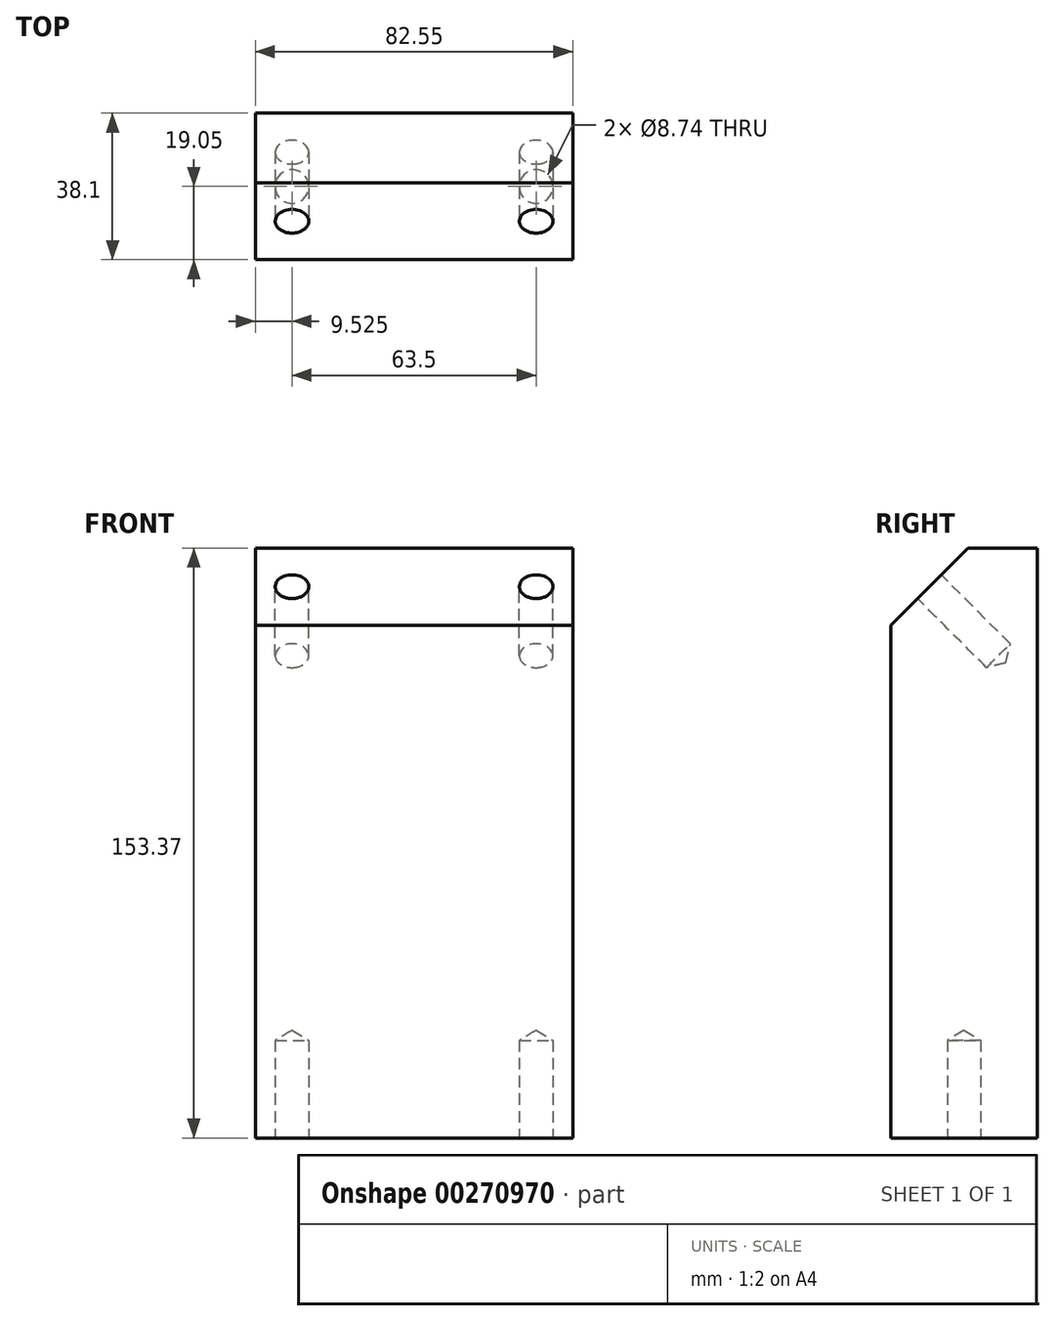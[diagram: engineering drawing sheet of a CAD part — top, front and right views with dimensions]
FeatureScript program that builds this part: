
annotation { "Feature Type Name" : "Feature", "Feature Type Description" : "" }
export const myFeature = defineFeature(function(context is Context, id is Id, definition is map)
    precondition{}
    {
        {
            var Q0;
            Q0=qCreatedBy(makeId("Top.planeOp"),FACE);
            var sketch = newSketch(context, id + "F0", { "sketchPlane" : qUnion([Q0])});
            skLineSegment(sketch, "E0", {"start": v(0, 0) * mm, "end": v(0, 38.1) * mm});
            skLineSegment(sketch, "E1", {"start": v(0, 38.1) * mm, "end": v(82.55, 38.1) * mm});
            skLineSegment(sketch, "E2", {"start": v(82.55, 38.1) * mm, "end": v(82.55, 0) * mm});
            skLineSegment(sketch, "E3", {"start": v(82.55, 0) * mm, "end": v(0, 0) * mm});
            skSolve(sketch);
        }
        {
            var Q0;
            Q0 = qSketchRegion(id + "F0", true);
            extrude(context, id + "F1", {"entities" : qUnion([Q0]), "depth" : 153.37 * mm});
        }
        {
            var Q0;
            Q0=makeQuery(id+"F1.opExtrude","CAP_EDGE",EDGE,{"disambiguationData":[OSD([sQuery(id+"F0.wireOp",EDGE,"E3")])],"isStart":false});
            chamfer(context, id + "F2", {"entities" : qUnion([Q0]), "chamferType" : ChamferType.OFFSET_ANGLE, "width" : 20.02 * mm, "oppositeDirection" : false, "angle" : 45 * degree, "tangentPropagation" : true});
        }
        {
            var Q0;
            Q0=makeQuery(id+"F2.opChamfer","BLEND_FACE",FACE,{"disambiguationData":[OSD([sQuery(id+"F0.wireOp",EDGE,"E3")])]});
            var sketch = newSketch(context, id + "F3", { "sketchPlane" : qUnion([Q0])});
            skPoint(sketch, "E4", {"position": v(9.53, 108.45) * mm});
            skPoint(sketch, "E5", {"position": v(73.03, 108.45) * mm});
            skSolve(sketch);
        }
        {
            var Q0;
            Q0=sQuery(id+"F3.wireOp",VERTEX,"E4");
            var Q1;
            Q1=sQuery(id+"F3.wireOp",VERTEX,"E5");
            var Q2;
            Q2=makeQuery(id+"F1.opExtrude","SWEPT_BODY",BODY,{"disambiguationData":[OSD([sQuery(id+"F0.wireOp",EDGE,"E0"),sQuery(id+"F0.wireOp",EDGE,"E1"),sQuery(id+"F0.wireOp",EDGE,"E2"),sQuery(id+"F0.wireOp",EDGE,"E3")])]});
            hole(context, id + "F4", {"style" : HoleStyle.SIMPLE, "endStyle" : HoleEndStyle.BLIND, "holeDiameter" : 8.74 * mm, "holeDepth" : 25.4 * mm, "tappedDepth" : 12.7 * mm, "tapClearance" : 3, "locations" : qUnion([Q0, Q1]), "scope" : qUnion([Q2])});
        }
        {
            var Q0;
            Q0=makeQuery(id+"F1.opExtrude","CAP_FACE",FACE,{"disambiguationData":[OSD([sQuery(id+"F0.wireOp",EDGE,"E0"),sQuery(id+"F0.wireOp",EDGE,"E1"),sQuery(id+"F0.wireOp",EDGE,"E2"),sQuery(id+"F0.wireOp",EDGE,"E3")])],"isStart":true});
            var sketch = newSketch(context, id + "F5", { "sketchPlane" : qUnion([Q0])});
            skPoint(sketch, "E6", {"position": v(9.53, -19.05) * mm});
            skPoint(sketch, "E7", {"position": v(73.03, -19.05) * mm});
            skSolve(sketch);
        }
        {
            var Q0;
            Q0=sQuery(id+"F5.wireOp",VERTEX,"E6");
            var Q1;
            Q1=sQuery(id+"F5.wireOp",VERTEX,"E7");
            var Q2;
            Q2=makeQuery(id+"F1.opExtrude","SWEPT_BODY",BODY,{"disambiguationData":[OSD([sQuery(id+"F0.wireOp",EDGE,"E0"),sQuery(id+"F0.wireOp",EDGE,"E1"),sQuery(id+"F0.wireOp",EDGE,"E2"),sQuery(id+"F0.wireOp",EDGE,"E3")])]});
            hole(context, id + "F6", {"style" : HoleStyle.SIMPLE, "endStyle" : HoleEndStyle.BLIND, "holeDiameter" : 8.74 * mm, "holeDepth" : 25.4 * mm, "tappedDepth" : 12.7 * mm, "tapClearance" : 3, "locations" : qUnion([Q0, Q1]), "scope" : qUnion([Q2])});
        }
    });
